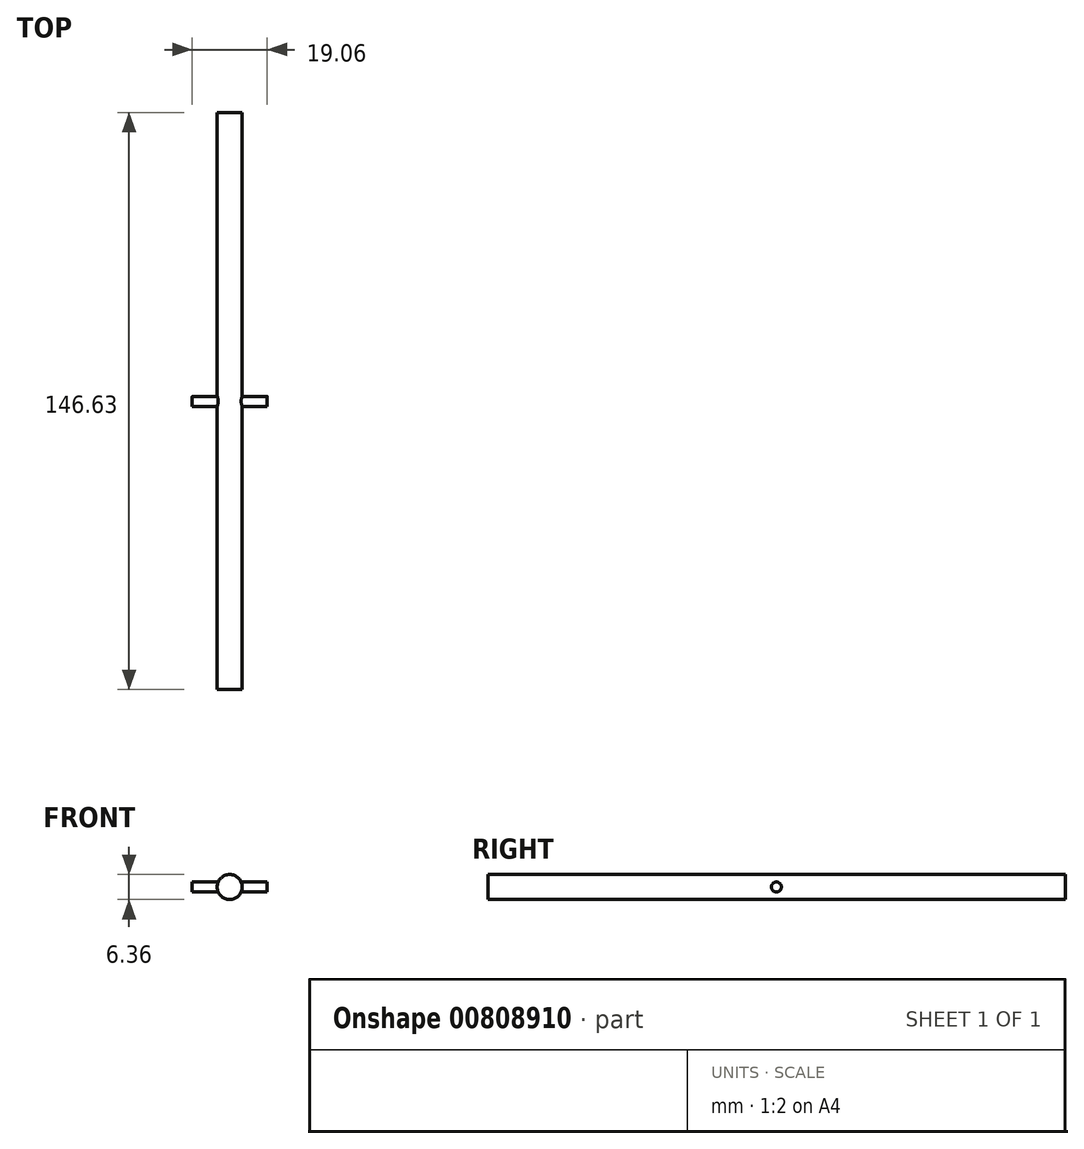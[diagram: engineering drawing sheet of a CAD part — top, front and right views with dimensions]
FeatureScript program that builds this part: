
annotation { "Feature Type Name" : "Feature", "Feature Type Description" : "" }
export const myFeature = defineFeature(function(context is Context, id is Id, definition is map)
    precondition{}
    {
        {
            var Q0;
            Q0=qCreatedBy(makeId("Front.planeOp"),FACE);
            var sketch = newSketch(context, id + "F0", { "sketchPlane" : qUnion([Q0])});
            skCircle(sketch, "E0", {"center": v(0, 0) * mm, "radius": 3.18 * mm});
            skSolve(sketch);
        }
        {
            var Q0;
            Q0 = qSketchRegion(id + "F0", true);
            extrude(context, id + "F1", {"entities" : qUnion([Q0]), "depth" : 146.63 * mm, "offsetDistance" : 25.4 * mm});
        }
        {
            var Q0;
            Q0=qCreatedBy(makeId("Right.planeOp"),FACE);
            var sketch = newSketch(context, id + "F2", { "sketchPlane" : qUnion([Q0])});
            skCircle(sketch, "E1", {"center": v(-73.4, 0) * mm, "radius": 1.27 * mm});
            skSolve(sketch);
        }
        {
            var Q0;
            Q0 = qSketchRegion(id + "F2", true);
            extrude(context, id + "F3", {"entities" : qUnion([Q0]), "operationType" : NewBodyOperationType.ADD, "endBound" : BoundingType.SYMMETRIC, "depth" : 19.05 * mm, "offsetDistance" : 25.4 * mm});
        }
    });
